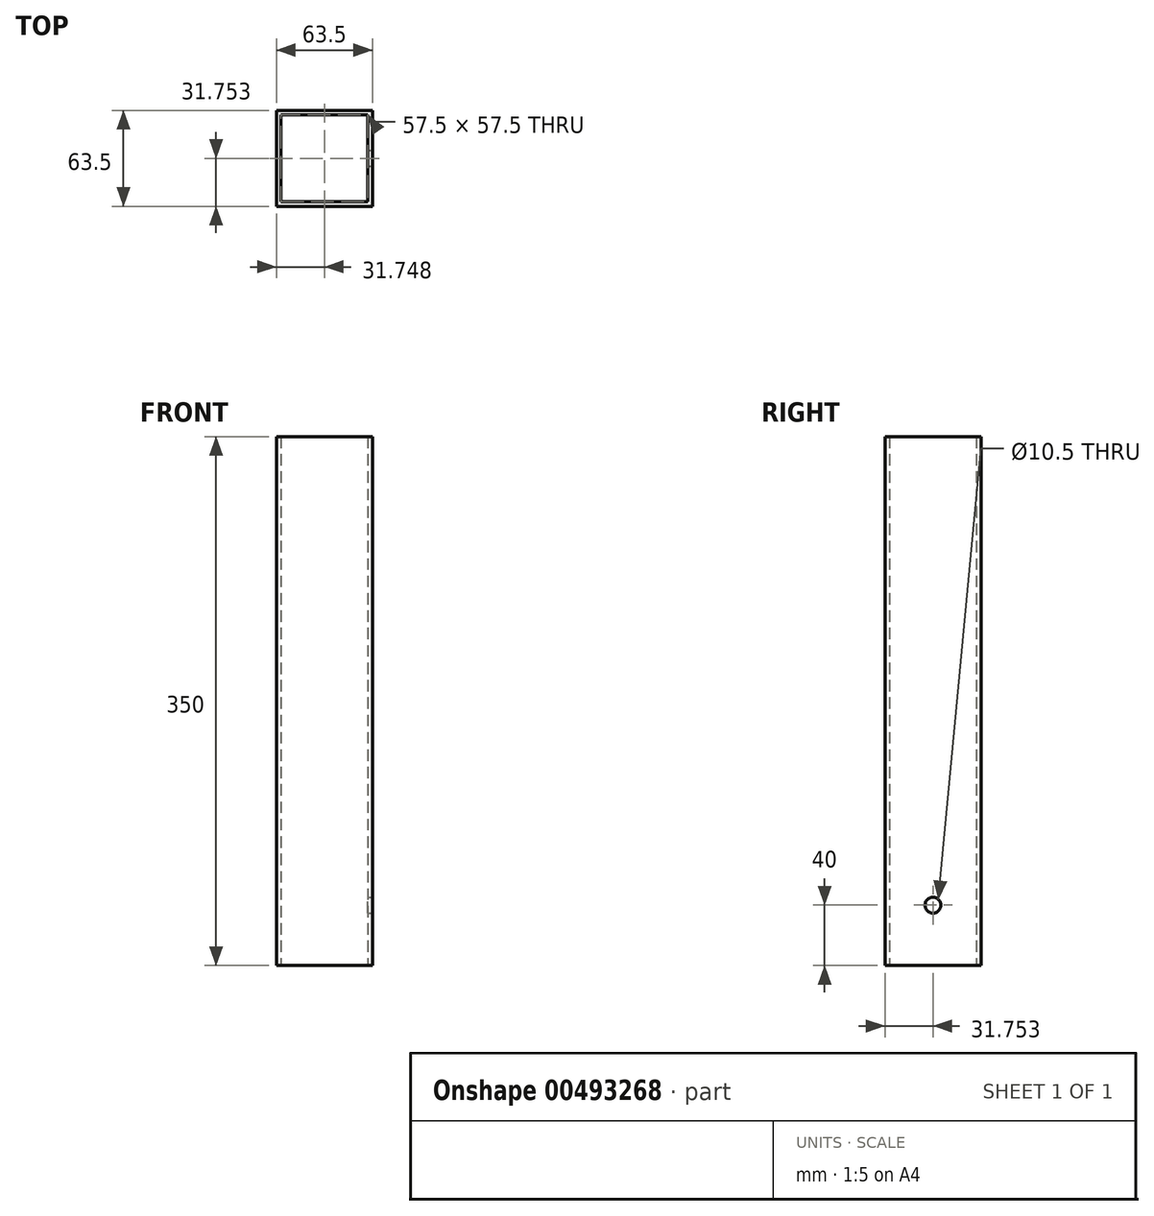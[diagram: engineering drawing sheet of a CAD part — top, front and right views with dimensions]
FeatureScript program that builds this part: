
annotation { "Feature Type Name" : "Feature", "Feature Type Description" : "" }
export const myFeature = defineFeature(function(context is Context, id is Id, definition is map)
    precondition{}
    {
        {
            var Q0;
            Q0=qCreatedBy(makeId("Top.planeOp"),FACE);
            var sketch = newSketch(context, id + "F0", { "sketchPlane" : qUnion([Q0])});
            skLineSegment(sketch, "E0.bottom", {"start": v(-26.21, 26.23) * mm, "end": v(31.29, 26.23) * mm});
            skLineSegment(sketch, "E0.top", {"start": v(-26.21, -31.27) * mm, "end": v(31.29, -31.27) * mm});
            skLineSegment(sketch, "E0.left", {"start": v(-26.21, 26.23) * mm, "end": v(-26.21, -31.27) * mm});
            skLineSegment(sketch, "E0.right", {"start": v(31.29, 26.23) * mm, "end": v(31.29, -31.27) * mm});
            skLineSegment(sketch, "E1.bottom", {"start": v(-29.21, 29.23) * mm, "end": v(34.29, 29.23) * mm});
            skLineSegment(sketch, "E1.top", {"start": v(-29.21, -34.27) * mm, "end": v(34.29, -34.27) * mm});
            skLineSegment(sketch, "E1.left", {"start": v(-29.21, 29.23) * mm, "end": v(-29.21, -34.27) * mm});
            skLineSegment(sketch, "E1.right", {"start": v(34.29, 29.23) * mm, "end": v(34.29, -34.27) * mm});
            skSolve(sketch);
        }
        {
            var Q0;
            Q0=qSketchRegion(id+"F0",true);
            extrude(context, id + "F1", {"entities" : qUnion([Q0]), "depth" : 350 * mm});
        }
        {
            var Q0;
            Q0=makeQuery(id+"F1.opExtrude","SWEPT_FACE",FACE,{"disambiguationData":[OSD([sQuery(id+"F0.wireOp",EDGE,"E1.right")])]});
            var sketch = newSketch(context, id + "F2", { "sketchPlane" : qUnion([Q0])});
            skCircle(sketch, "E2", {"center": v(-2.52, 40) * mm, "radius": 5.25 * mm});
            skSolve(sketch);
        }
        {
            var Q0;
            Q0 = qSketchRegion(id + "F2", true);
            extrude(context, id + "F3", {"entities" : qUnion([Q0]), "operationType" : NewBodyOperationType.REMOVE, "oppositeDirection" : true, "depth" : 10 * mm, "offsetDistance" : 25 * mm});
        }
    });
